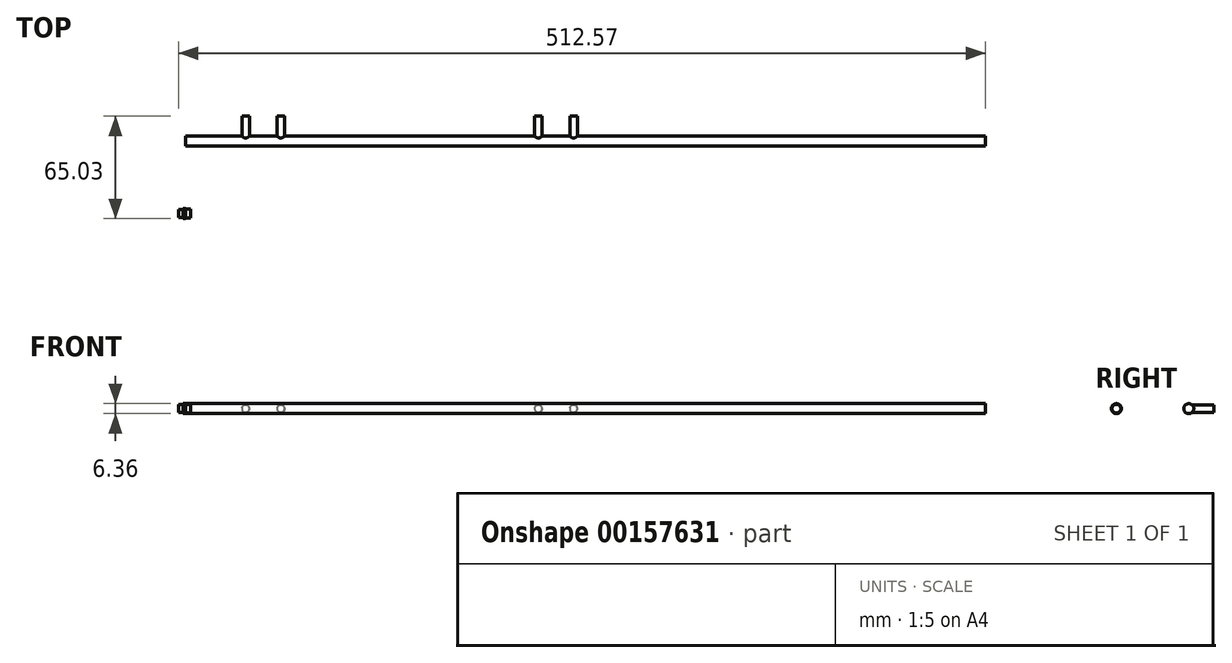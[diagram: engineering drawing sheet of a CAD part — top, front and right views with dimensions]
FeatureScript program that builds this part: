
annotation { "Feature Type Name" : "Feature", "Feature Type Description" : "" }
export const myFeature = defineFeature(function(context is Context, id is Id, definition is map)
    precondition{}
    {
        {
            var Q0;
            Q0=qCreatedBy(makeId("Right.planeOp"),FACE);
            var sketch = newSketch(context, id + "F0", { "sketchPlane" : qUnion([Q0])});
            skCircle(sketch, "E0", {"center": v(0, 0) * mm, "radius": 3.18 * mm});
            skSolve(sketch);
        }
        {
            var Q0;
            Q0=makeQuery(id+"F0.imprint","IMPRINT",FACE,{"disambiguationData":[TD([[makeQuery(id+"F0.imprint","IMPRINT",EDGE,{"derivedFrom":sQuery(id+"F0.wireOp",EDGE,"E0")}),1.0]])]});
            extrude(context, id + "F1", {"entities" : qUnion([Q0]), "depth" : 508 * mm});
        }
        {
            var Q0;
            Q0=qCreatedBy(makeId("Front.planeOp"),FACE);
            cPlane(context, id + "F2", {"entities" : qUnion([Q0]), "cplaneType" : CPlaneType.OFFSET, "offset" : 3.17 * mm, "oppositeDirection" : true, "width" : 152.4 * mm, "height" : 152.4 * mm});
        }
        {
            var Q0;
            Q0=qCreatedBy(id+"F2.planeOp",FACE);
            var sketch = newSketch(context, id + "F3", { "sketchPlane" : qUnion([Q0])});
            skLineSegment(sketch, "E1", {"start": v(0, 0) * mm, "end": v(508.56, 0) * mm, "construction": true});
            skCircle(sketch, "E2", {"center": v(38.1, 0) * mm, "radius": 2.39 * mm});
            skCircle(sketch, "E3", {"center": v(60.45, 0) * mm, "radius": 2.39 * mm});
            skCircle(sketch, "E4", {"center": v(224.03, 0) * mm, "radius": 2.39 * mm});
            skCircle(sketch, "E5", {"center": v(246.38, 0) * mm, "radius": 2.39 * mm});
            skSolve(sketch);
        }
        {
            var Q0;
            Q0=makeQuery(id+"F3.imprint","IMPRINT",FACE,{"disambiguationData":[TD([[makeQuery(id+"F3.imprint","IMPRINT",EDGE,{"derivedFrom":sQuery(id+"F3.wireOp",EDGE,"E5")}),1.0]])]});
            var Q1;
            Q1=makeQuery(id+"F3.imprint","IMPRINT",FACE,{"disambiguationData":[TD([[makeQuery(id+"F3.imprint","IMPRINT",EDGE,{"derivedFrom":sQuery(id+"F3.wireOp",EDGE,"E4")}),1.0]])]});
            var Q2;
            Q2=makeQuery(id+"F3.imprint","IMPRINT",FACE,{"disambiguationData":[TD([[makeQuery(id+"F3.imprint","IMPRINT",EDGE,{"derivedFrom":sQuery(id+"F3.wireOp",EDGE,"E3")}),1.0]])]});
            var Q3;
            Q3=makeQuery(id+"F3.imprint","IMPRINT",FACE,{"disambiguationData":[TD([[makeQuery(id+"F3.imprint","IMPRINT",EDGE,{"derivedFrom":sQuery(id+"F3.wireOp",EDGE,"E2")}),1.0]])]});
            extrude(context, id + "F4", {"entities" : qUnion([Q0, Q1, Q2, Q3]), "operationType" : NewBodyOperationType.ADD, "depth" : 2.54 * mm, "hasSecondDirection" : true, "secondDirectionOppositeDirection" : true, "secondDirectionDepth" : 12.7 * mm});
        }
        {
            var Q0;
            Q0=qCreatedBy(makeId("Right.planeOp"),FACE);
            var sketch = newSketch(context, id + "F5", { "sketchPlane" : qUnion([Q0])});
            skCircle(sketch, "E6", {"center": v(-45.98, 0) * mm, "radius": 3.18 * mm});
            skSolve(sketch);
        }
        {
            var Q0;
            Q0=makeQuery(id+"F5.imprint","IMPRINT",FACE,{"disambiguationData":[TD([[makeQuery(id+"F5.imprint","IMPRINT",EDGE,{"derivedFrom":sQuery(id+"F5.wireOp",EDGE,"E6")}),1.0]])]});
            extrude(context, id + "F6", {"entities" : qUnion([Q0]), "oppositeDirection" : true, "depth" : 1.52 * mm});
        }
        {
            var Q0;
            Q0=makeQuery(id+"F6.opExtrude","CAP_FACE",FACE,{"disambiguationData":[OSD([sQuery(id+"F5.wireOp",EDGE,"E6")])],"isStart":true});
            var sketch = newSketch(context, id + "F7", { "sketchPlane" : qUnion([Q0])});
            skCircle(sketch, "E7", {"center": v(-45.98, 0) * mm, "radius": 2.8 * mm});
            skSolve(sketch);
        }
        {
            var Q0;
            Q0=makeQuery(id+"F7.imprint","IMPRINT",FACE,{"disambiguationData":[TD([[makeQuery(id+"F7.imprint","IMPRINT",EDGE,{"derivedFrom":sQuery(id+"F7.wireOp",EDGE,"E7")}),1.0]])]});
            extrude(context, id + "F8", {"entities" : qUnion([Q0]), "operationType" : NewBodyOperationType.ADD, "depth" : 3.3 * mm});
        }
        {
            var Q0;
            Q0=makeQuery(id+"F6.opExtrude","CAP_FACE",FACE,{"disambiguationData":[OSD([sQuery(id+"F5.wireOp",EDGE,"E6")])],"isStart":false});
            var sketch = newSketch(context, id + "F9", { "sketchPlane" : qUnion([Q0])});
            skCircle(sketch, "E8", {"center": v(45.98, 0) * mm, "radius": 2.54 * mm});
            skSolve(sketch);
        }
        {
            var Q0;
            Q0=makeQuery(id+"F9.imprint","IMPRINT",FACE,{"disambiguationData":[TD([[makeQuery(id+"F9.imprint","IMPRINT",EDGE,{"derivedFrom":sQuery(id+"F9.wireOp",EDGE,"E8")}),1.0]])]});
            extrude(context, id + "F10", {"entities" : qUnion([Q0]), "operationType" : NewBodyOperationType.ADD, "depth" : 3.05 * mm});
        }
    });
